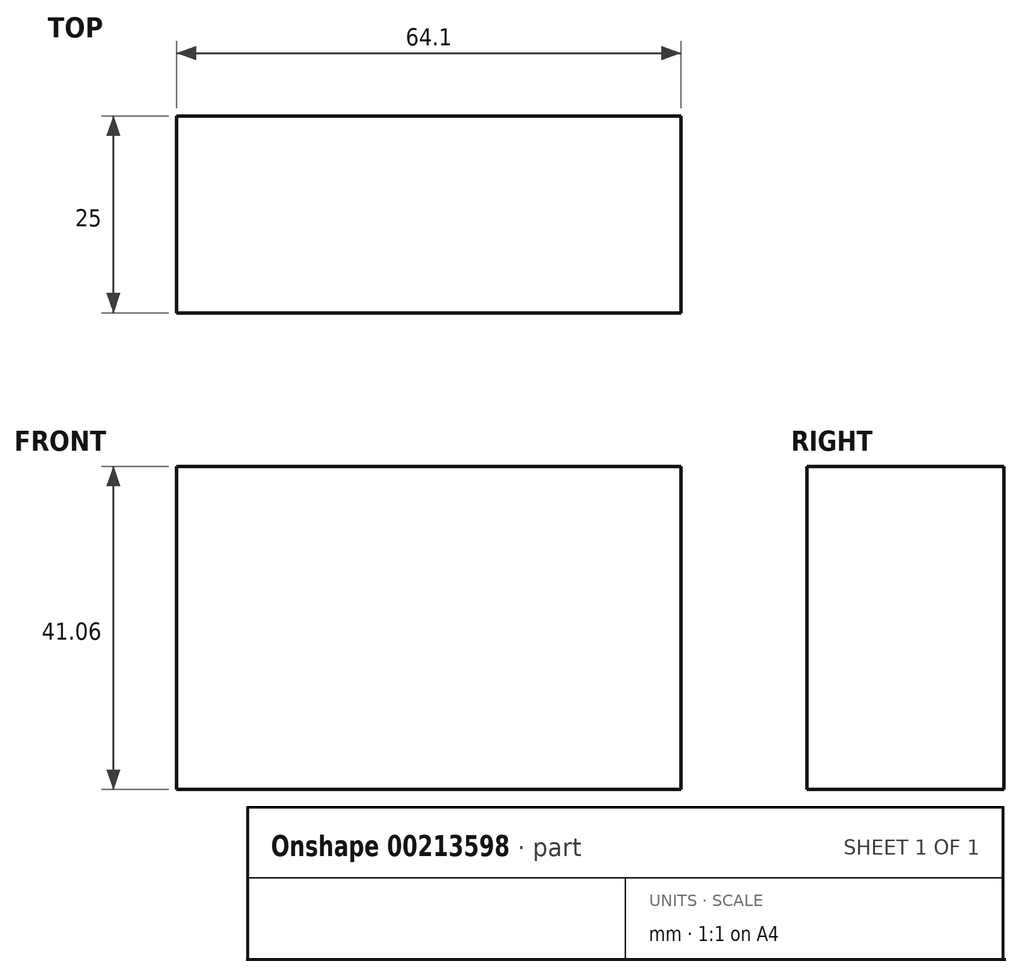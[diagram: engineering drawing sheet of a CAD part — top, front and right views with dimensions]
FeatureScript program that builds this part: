
annotation { "Feature Type Name" : "Feature", "Feature Type Description" : "" }
export const myFeature = defineFeature(function(context is Context, id is Id, definition is map)
    precondition{}
    {
        {
            var Q0;
            Q0=qCreatedBy(makeId("Front.planeOp"),FACE);
            var sketch = newSketch(context, id + "F0", { "sketchPlane" : qUnion([Q0])});
            skLineSegment(sketch, "E0.bottom", {"start": v(-28.81, 19.45) * mm, "end": v(35.3, 19.45) * mm});
            skLineSegment(sketch, "E0.top", {"start": v(-28.81, -21.6) * mm, "end": v(35.3, -21.6) * mm});
            skLineSegment(sketch, "E0.left", {"start": v(-28.81, 19.45) * mm, "end": v(-28.81, -21.6) * mm});
            skLineSegment(sketch, "E0.right", {"start": v(35.3, 19.45) * mm, "end": v(35.3, -21.6) * mm});
            skSolve(sketch);
        }
        {
            var Q0;
            Q0=makeQuery(id+"F0.imprint","IMPRINT",FACE,{"disambiguationData":[TD([[makeQuery(id+"F0.imprint","IMPRINT",EDGE,{"derivedFrom":sQuery(id+"F0.wireOp",EDGE,"E0.bottom")}),-1.0]])]});
            extrude(context, id + "F1", {"entities" : qUnion([Q0]), "endBound" : BoundingType.SYMMETRIC, "depth" : 25 * mm});
        }
    });
